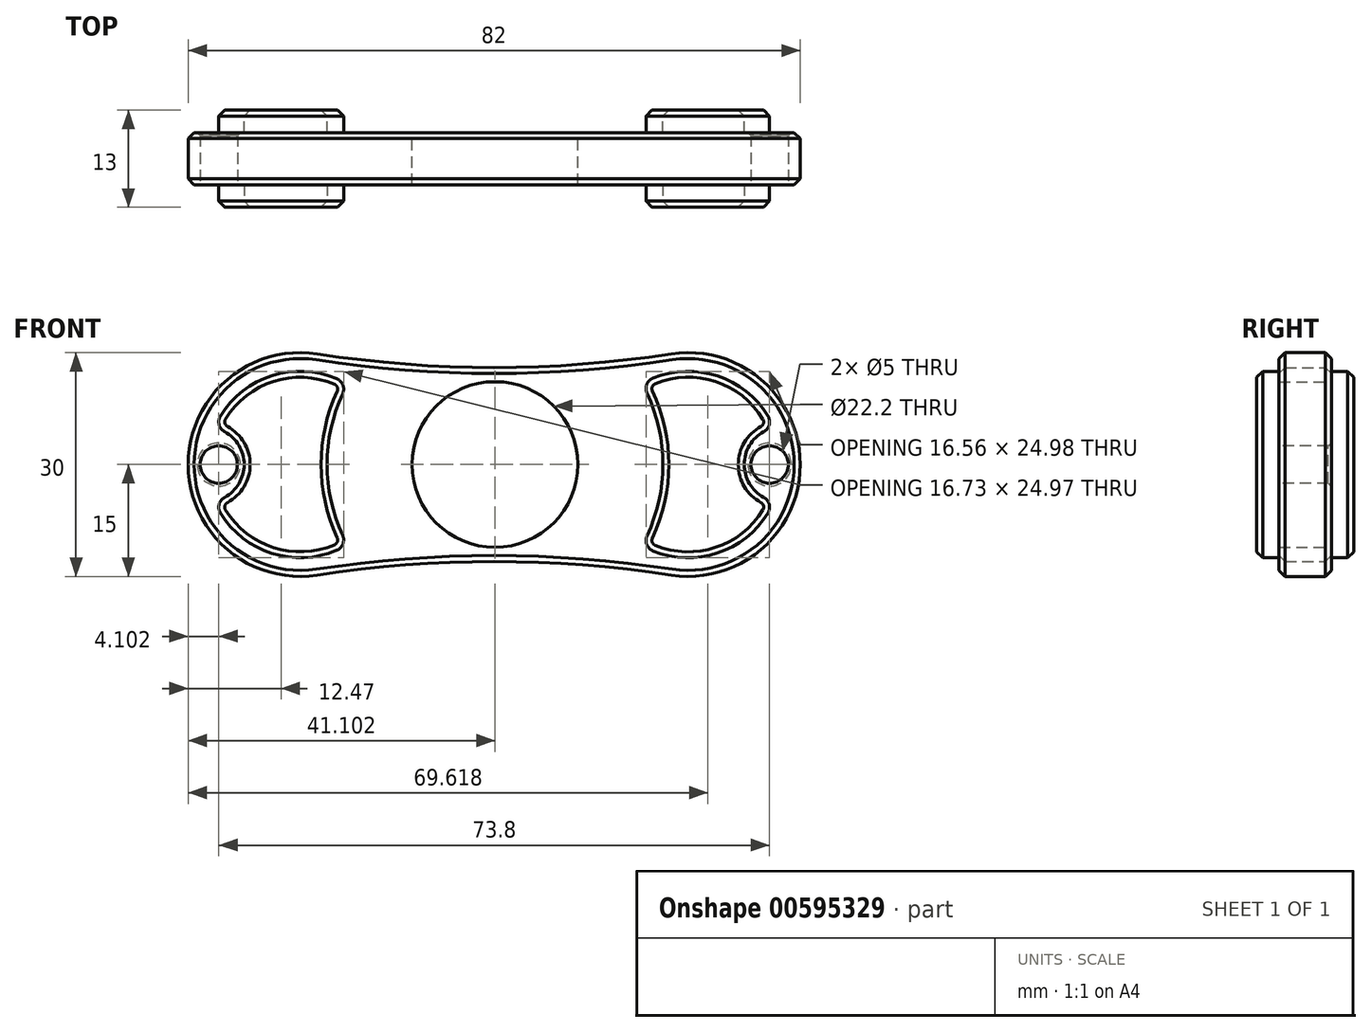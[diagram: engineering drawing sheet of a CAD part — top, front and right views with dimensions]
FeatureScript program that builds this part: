
annotation { "Feature Type Name" : "Feature", "Feature Type Description" : "" }
export const myFeature = defineFeature(function(context is Context, id is Id, definition is map)
    precondition{}
    {
        {
            var Q0;
            Q0=qCreatedBy(makeId("Front.planeOp"),FACE);
            var sketch = newSketch(context, id + "F0", { "sketchPlane" : qUnion([Q0])});
            skCircle(sketch, "E0", {"center": v(-1.84, 0) * mm, "radius": 11.1 * mm});
            skArc(sketch, "E1", {"start": v(-25.64, 14.82) * mm, "mid": v(-42.94, 0) * mm, "end": v(-25.64, -14.82) * mm});
            skArc(sketch, "E2", {"start": v(-25.64, 14.82) * mm, "mid": v(-1.94, 13) * mm, "end": v(21.77, 14.82) * mm});
            skArc(sketch, "E3", {"start": v(21.77, -14.82) * mm, "mid": v(-1.94, -13) * mm, "end": v(-25.64, -14.82) * mm});
            skArc(sketch, "E4.trimOffspring", {"start": v(21.77, -14.82) * mm, "mid": v(39.06, 0) * mm, "end": v(21.77, 14.82) * mm});
            skSolve(sketch);
        }
        {
            var Q0;
            Q0=makeQuery(id+"F0.imprint","IMPRINT",FACE,{"disambiguationData":[TD([[makeQuery(id+"F0.imprint","IMPRINT",EDGE,{"derivedFrom":sQuery(id+"F0.wireOp",EDGE,"E0")}),-1.0]])]});
            extrude(context, id + "F1", {"entities" : qUnion([Q0]), "depth" : 7 * mm, "offsetDistance" : 25 * mm});
        }
        {
            var Q0;
            Q0=makeQuery(id+"F1.opExtrude","CAP_EDGE",EDGE,{"disambiguationData":[OSD([sQuery(id+"F0.wireOp",EDGE,"E1")])],"isStart":false});
            var Q1;
            Q1=makeQuery(id+"F1.opExtrude","CAP_EDGE",EDGE,{"disambiguationData":[OSD([sQuery(id+"F0.wireOp",EDGE,"E3")])],"isStart":false});
            var Q2;
            Q2=makeQuery(id+"F1.opExtrude","CAP_EDGE",EDGE,{"disambiguationData":[OSD([sQuery(id+"F0.wireOp",EDGE,"E3")])],"isStart":true});
            chamfer(context, id + "F2", {"entities" : qUnion([Q0, Q1, Q2]), "width" : .8 * mm, "tangentPropagation" : true});
        }
        {
            var Q0;
            Q0=makeQuery(id+"F1.opExtrude","CAP_FACE",FACE,{"disambiguationData":[OSD([sQuery(id+"F0.wireOp",EDGE,"E0"),sQuery(id+"F0.wireOp",EDGE,"E1"),sQuery(id+"F0.wireOp",EDGE,"E2"),sQuery(id+"F0.wireOp",EDGE,"E3"),sQuery(id+"F0.wireOp",EDGE,"E4.trimOffspring")])],"isStart":false});
            var sketch = newSketch(context, id + "F3", { "sketchPlane" : qUnion([Q0])});
            skCircle(sketch, "E5", {"center": v(-27.94, 0) * mm, "radius": 12.5 * mm});
            skCircle(sketch, "E6", {"center": v(24.06, 0) * mm, "radius": 12.5 * mm});
            skSolve(sketch);
        }
        {
            var Q0;
            Q0=qSketchRegion(id+"F3",true);
            extrude(context, id + "F4", {"entities" : qUnion([Q0]), "operationType" : NewBodyOperationType.ADD, "depth" : 3 * mm, "offsetDistance" : 25 * mm});
        }
        {
            var Q0;
            Q0=makeQuery(id+"F1.opExtrude","CAP_FACE",FACE,{"disambiguationData":[OSD([sQuery(id+"F0.wireOp",EDGE,"E0"),sQuery(id+"F0.wireOp",EDGE,"E1"),sQuery(id+"F0.wireOp",EDGE,"E2"),sQuery(id+"F0.wireOp",EDGE,"E3"),sQuery(id+"F0.wireOp",EDGE,"E4.trimOffspring")])],"isStart":true});
            var sketch = newSketch(context, id + "F5", { "sketchPlane" : qUnion([Q0])});
            skCircle(sketch, "E7", {"center": v(-24.06, 0) * mm, "radius": 12.5 * mm});
            skCircle(sketch, "E8", {"center": v(27.94, 0) * mm, "radius": 12.5 * mm});
            skSolve(sketch);
        }
        {
            var Q0;
            Q0=qSketchRegion(id+"F5",true);
            extrude(context, id + "F6", {"entities" : qUnion([Q0]), "operationType" : NewBodyOperationType.ADD, "depth" : 3 * mm, "offsetDistance" : 25 * mm});
        }
        {
            var Q0;
            Q0=makeQuery(id+"F4.opExtrude","CAP_FACE",FACE,{"disambiguationData":[OSD([sQuery(id+"F3.wireOp",EDGE,"E6")])],"isStart":false});
            var sketch = newSketch(context, id + "F7", { "sketchPlane" : qUnion([Q0])});
            skSolve(sketch);
        }
        {
            var Q0;
            Q0=makeQuery(id+"F4.opExtrude","CAP_FACE",FACE,{"disambiguationData":[OSD([sQuery(id+"F3.wireOp",EDGE,"E5")])],"isStart":false});
            var sketch = newSketch(context, id + "F8", { "sketchPlane" : qUnion([Q0])});
            skCircle(sketch, "E9", {"center": v(-1.84, 0) * mm, "radius": 22.5 * mm});
            skSolve(sketch);
        }
        {
            var Q0;
            Q0=qSketchRegion(id+"F8",true);
            extrude(context, id + "F9", {"entities" : qUnion([Q0]), "operationType" : NewBodyOperationType.REMOVE, "oppositeDirection" : true, "depth" : 3 * mm, "offsetDistance" : 25 * mm});
        }
        {
            var Q0;
            Q0=makeQuery(id+"F6.opExtrude","CAP_FACE",FACE,{"disambiguationData":[OSD([sQuery(id+"F5.wireOp",EDGE,"E7")])],"isStart":false});
            var sketch = newSketch(context, id + "F10", { "sketchPlane" : qUnion([Q0])});
            skCircle(sketch, "E10", {"center": v(1.84, 0) * mm, "radius": 22.5 * mm});
            skSolve(sketch);
        }
        {
            var Q0;
            Q0=qSketchRegion(id+"F10",true);
            extrude(context, id + "F11", {"entities" : qUnion([Q0]), "operationType" : NewBodyOperationType.REMOVE, "oppositeDirection" : true, "depth" : 3 * mm, "offsetDistance" : 25 * mm});
        }
        {
            var Q0;
            Q0=makeQuery(id+"F6.opExtrude","CAP_FACE",FACE,{"disambiguationData":[OSD([sQuery(id+"F5.wireOp",EDGE,"E7")])],"isStart":false});
            var sketch = newSketch(context, id + "F12", { "sketchPlane" : qUnion([Q0])});
            skCircle(sketch, "E11", {"center": v(-36.56, 0) * mm, "radius": 5 * mm});
            skSolve(sketch);
        }
        {
            var Q0;
            Q0=qSketchRegion(id+"F12",true);
            extrude(context, id + "F13", {"entities" : qUnion([Q0]), "operationType" : NewBodyOperationType.REMOVE, "oppositeDirection" : true, "depth" : 3 * mm, "offsetDistance" : 25 * mm});
        }
        {
            var Q0;
            Q0=makeQuery(id+"F6.opExtrude","CAP_FACE",FACE,{"disambiguationData":[OSD([sQuery(id+"F5.wireOp",EDGE,"E8")])],"isStart":false});
            var sketch = newSketch(context, id + "F14", { "sketchPlane" : qUnion([Q0])});
            skCircle(sketch, "E12", {"center": v(40.44, 0) * mm, "radius": 5 * mm});
            skSolve(sketch);
        }
        {
            var Q0;
            Q0=qSketchRegion(id+"F14",true);
            extrude(context, id + "F15", {"entities" : qUnion([Q0]), "operationType" : NewBodyOperationType.REMOVE, "oppositeDirection" : true, "depth" : 3 * mm, "offsetDistance" : 25 * mm});
        }
        {
            var Q0;
            Q0=makeQuery(id+"F4.opExtrude","CAP_FACE",FACE,{"disambiguationData":[OSD([sQuery(id+"F3.wireOp",EDGE,"E5")])],"isStart":false});
            var sketch = newSketch(context, id + "F16", { "sketchPlane" : qUnion([Q0])});
            skCircle(sketch, "E13", {"center": v(-40.44, 0) * mm, "radius": 5 * mm});
            skSolve(sketch);
        }
        {
            var Q0;
            Q0=qSketchRegion(id+"F16",true);
            extrude(context, id + "F17", {"entities" : qUnion([Q0]), "operationType" : NewBodyOperationType.REMOVE, "oppositeDirection" : true, "depth" : 3 * mm, "offsetDistance" : 25 * mm});
        }
        {
            var Q0;
            Q0=makeQuery(id+"F7.imprint","IMPRINT",FACE,{"disambiguationData":[TD([[makeQuery(id+"F7.imprint","IMPRINT",EDGE,{"derivedFrom":makeQuery(id+"F4.opExtrude","CAP_EDGE",EDGE,{"disambiguationData":[OSD([sQuery(id+"F3.wireOp",EDGE,"E6")])],"isStart":false})}),1.0]])]});
            var sketch = newSketch(context, id + "F18", { "sketchPlane" : qUnion([Q0])});
            skCircle(sketch, "E14", {"center": v(36.56, 0) * mm, "radius": 5 * mm});
            skSolve(sketch);
        }
        {
            var Q0;
            Q0=qSketchRegion(id+"F18",true);
            extrude(context, id + "F19", {"entities" : qUnion([Q0]), "operationType" : NewBodyOperationType.REMOVE, "oppositeDirection" : true, "depth" : 3 * mm, "offsetDistance" : 25 * mm});
        }
        {
            var Q0;
            Q0=makeQuery(id+"F17.boolean.opBoolean","INTERSECT",EDGE,{"disambiguationData":[OD(0.0)],"derivedFrom":[makeQuery(id+"F4.opExtrude","SWEPT_FACE",FACE,{"disambiguationData":[OSD([sQuery(id+"F3.wireOp",EDGE,"E5")])]}),makeQuery(id+"F17.opExtrude","SWEPT_FACE",FACE,{"disambiguationData":[OSD([sQuery(id+"F16.wireOp",EDGE,"E13")])]})]});
            var Q1;
            Q1=makeQuery(id+"F17.boolean.opBoolean","INTERSECT",EDGE,{"disambiguationData":[OD(1.0)],"derivedFrom":[makeQuery(id+"F4.opExtrude","SWEPT_FACE",FACE,{"disambiguationData":[OSD([sQuery(id+"F3.wireOp",EDGE,"E5")])]}),makeQuery(id+"F17.opExtrude","SWEPT_FACE",FACE,{"disambiguationData":[OSD([sQuery(id+"F16.wireOp",EDGE,"E13")])]})]});
            var Q2;
            Q2=makeQuery(id+"F9.boolean.opBoolean","INTERSECT",EDGE,{"disambiguationData":[OD(1.0)],"derivedFrom":[makeQuery(id+"F4.opExtrude","SWEPT_FACE",FACE,{"disambiguationData":[OSD([sQuery(id+"F3.wireOp",EDGE,"E5")])]}),makeQuery(id+"F9.opExtrude","SWEPT_FACE",FACE,{"disambiguationData":[OSD([sQuery(id+"F8.wireOp",EDGE,"E9")])]})]});
            var Q3;
            Q3=makeQuery(id+"F9.boolean.opBoolean","INTERSECT",EDGE,{"disambiguationData":[OD(0.0)],"derivedFrom":[makeQuery(id+"F4.opExtrude","SWEPT_FACE",FACE,{"disambiguationData":[OSD([sQuery(id+"F3.wireOp",EDGE,"E5")])]}),makeQuery(id+"F9.opExtrude","SWEPT_FACE",FACE,{"disambiguationData":[OSD([sQuery(id+"F8.wireOp",EDGE,"E9")])]})]});
            var Q4;
            Q4=makeQuery(id+"F9.boolean.opBoolean","INTERSECT",EDGE,{"disambiguationData":[OD(1.0)],"derivedFrom":[makeQuery(id+"F4.opExtrude","SWEPT_FACE",FACE,{"disambiguationData":[OSD([sQuery(id+"F3.wireOp",EDGE,"E6")])]}),makeQuery(id+"F9.opExtrude","SWEPT_FACE",FACE,{"disambiguationData":[OSD([sQuery(id+"F8.wireOp",EDGE,"E9")])]})]});
            var Q5;
            Q5=makeQuery(id+"F9.boolean.opBoolean","INTERSECT",EDGE,{"disambiguationData":[OD(0.0)],"derivedFrom":[makeQuery(id+"F4.opExtrude","SWEPT_FACE",FACE,{"disambiguationData":[OSD([sQuery(id+"F3.wireOp",EDGE,"E6")])]}),makeQuery(id+"F9.opExtrude","SWEPT_FACE",FACE,{"disambiguationData":[OSD([sQuery(id+"F8.wireOp",EDGE,"E9")])]})]});
            var Q6;
            Q6=makeQuery(id+"F19.boolean.opBoolean","INTERSECT",EDGE,{"disambiguationData":[OD(1.0)],"derivedFrom":[makeQuery(id+"F4.opExtrude","SWEPT_FACE",FACE,{"disambiguationData":[OSD([sQuery(id+"F3.wireOp",EDGE,"E6")])]}),makeQuery(id+"F19.opExtrude","SWEPT_FACE",FACE,{"disambiguationData":[OSD([sQuery(id+"F18.wireOp",EDGE,"E14")])]})]});
            var Q7;
            Q7=makeQuery(id+"F19.boolean.opBoolean","INTERSECT",EDGE,{"disambiguationData":[OD(0.0)],"derivedFrom":[makeQuery(id+"F4.opExtrude","SWEPT_FACE",FACE,{"disambiguationData":[OSD([sQuery(id+"F3.wireOp",EDGE,"E6")])]}),makeQuery(id+"F19.opExtrude","SWEPT_FACE",FACE,{"disambiguationData":[OSD([sQuery(id+"F18.wireOp",EDGE,"E14")])]})]});
            var Q8;
            Q8=makeQuery(id+"F11.boolean.opBoolean","INTERSECT",EDGE,{"disambiguationData":[OD(0.0)],"derivedFrom":[makeQuery(id+"F6.opExtrude","SWEPT_FACE",FACE,{"disambiguationData":[OSD([sQuery(id+"F5.wireOp",EDGE,"E8")])]}),makeQuery(id+"F11.opExtrude","SWEPT_FACE",FACE,{"disambiguationData":[OSD([sQuery(id+"F10.wireOp",EDGE,"E10")])]})]});
            var Q9;
            Q9=makeQuery(id+"F11.boolean.opBoolean","INTERSECT",EDGE,{"disambiguationData":[OD(1.0)],"derivedFrom":[makeQuery(id+"F6.opExtrude","SWEPT_FACE",FACE,{"disambiguationData":[OSD([sQuery(id+"F5.wireOp",EDGE,"E8")])]}),makeQuery(id+"F11.opExtrude","SWEPT_FACE",FACE,{"disambiguationData":[OSD([sQuery(id+"F10.wireOp",EDGE,"E10")])]})]});
            var Q10;
            Q10=makeQuery(id+"F15.boolean.opBoolean","INTERSECT",EDGE,{"disambiguationData":[OD(0.0)],"derivedFrom":[makeQuery(id+"F6.opExtrude","SWEPT_FACE",FACE,{"disambiguationData":[OSD([sQuery(id+"F5.wireOp",EDGE,"E8")])]}),makeQuery(id+"F15.opExtrude","SWEPT_FACE",FACE,{"disambiguationData":[OSD([sQuery(id+"F14.wireOp",EDGE,"E12")])]})]});
            var Q11;
            Q11=makeQuery(id+"F15.boolean.opBoolean","INTERSECT",EDGE,{"disambiguationData":[OD(1.0)],"derivedFrom":[makeQuery(id+"F6.opExtrude","SWEPT_FACE",FACE,{"disambiguationData":[OSD([sQuery(id+"F5.wireOp",EDGE,"E8")])]}),makeQuery(id+"F15.opExtrude","SWEPT_FACE",FACE,{"disambiguationData":[OSD([sQuery(id+"F14.wireOp",EDGE,"E12")])]})]});
            var Q12;
            Q12=makeQuery(id+"F11.boolean.opBoolean","INTERSECT",EDGE,{"disambiguationData":[OD(0.0)],"derivedFrom":[makeQuery(id+"F6.opExtrude","SWEPT_FACE",FACE,{"disambiguationData":[OSD([sQuery(id+"F5.wireOp",EDGE,"E7")])]}),makeQuery(id+"F11.opExtrude","SWEPT_FACE",FACE,{"disambiguationData":[OSD([sQuery(id+"F10.wireOp",EDGE,"E10")])]})]});
            var Q13;
            Q13=makeQuery(id+"F11.boolean.opBoolean","INTERSECT",EDGE,{"disambiguationData":[OD(1.0)],"derivedFrom":[makeQuery(id+"F6.opExtrude","SWEPT_FACE",FACE,{"disambiguationData":[OSD([sQuery(id+"F5.wireOp",EDGE,"E7")])]}),makeQuery(id+"F11.opExtrude","SWEPT_FACE",FACE,{"disambiguationData":[OSD([sQuery(id+"F10.wireOp",EDGE,"E10")])]})]});
            var Q14;
            Q14=makeQuery(id+"F13.boolean.opBoolean","INTERSECT",EDGE,{"disambiguationData":[OD(0.0)],"derivedFrom":[makeQuery(id+"F6.opExtrude","SWEPT_FACE",FACE,{"disambiguationData":[OSD([sQuery(id+"F5.wireOp",EDGE,"E7")])]}),makeQuery(id+"F13.opExtrude","SWEPT_FACE",FACE,{"disambiguationData":[OSD([sQuery(id+"F12.wireOp",EDGE,"E11")])]})]});
            var Q15;
            Q15=makeQuery(id+"F13.boolean.opBoolean","INTERSECT",EDGE,{"disambiguationData":[OD(1.0)],"derivedFrom":[makeQuery(id+"F6.opExtrude","SWEPT_FACE",FACE,{"disambiguationData":[OSD([sQuery(id+"F5.wireOp",EDGE,"E7")])]}),makeQuery(id+"F13.opExtrude","SWEPT_FACE",FACE,{"disambiguationData":[OSD([sQuery(id+"F12.wireOp",EDGE,"E11")])]})]});
            fillet(context, id + "F20", {"entities" : qUnion([Q0, Q1, Q2, Q3, Q4, Q5, Q6, Q7, Q8, Q9, Q10, Q11, Q12, Q13, Q14, Q15]), "radius" : 1.5 * mm, "tangentPropagation" : true, "allowEdgeOverflow" : false});
        }
        {
            var Q0;
            Q0=makeQuery(id+"F19.boolean.opBoolean","MERGE",FACE,{"derivedFrom":[makeQuery(id+"F17.boolean.opBoolean","MERGE",FACE,{"derivedFrom":[makeQuery(id+"F9.boolean.opBoolean","MERGE",FACE,{"derivedFrom":[makeQuery(id+"F1.opExtrude","CAP_FACE",FACE,{"disambiguationData":[OSD([sQuery(id+"F0.wireOp",EDGE,"E0"),sQuery(id+"F0.wireOp",EDGE,"E1"),sQuery(id+"F0.wireOp",EDGE,"E2"),sQuery(id+"F0.wireOp",EDGE,"E3"),sQuery(id+"F0.wireOp",EDGE,"E4.trimOffspring")])],"isStart":false}),makeQuery(id+"F9.opExtrude","CAP_FACE",FACE,{"disambiguationData":[OSD([sQuery(id+"F8.wireOp",EDGE,"E9")])],"isStart":false})]}),makeQuery(id+"F17.opExtrude","CAP_FACE",FACE,{"disambiguationData":[OSD([sQuery(id+"F16.wireOp",EDGE,"E13")])],"isStart":false})]}),makeQuery(id+"F19.opExtrude","CAP_FACE",FACE,{"disambiguationData":[OSD([sQuery(id+"F18.wireOp",EDGE,"E14")])],"isStart":false})]});
            var sketch = newSketch(context, id + "F21", { "sketchPlane" : qUnion([Q0])});
            skCircle(sketch, "E15", {"center": v(-38.84, 0) * mm, "radius": 2.5 * mm});
            skSolve(sketch);
        }
        {
            var Q0;
            Q0=qSketchRegion(id+"F21",true);
            extrude(context, id + "F22", {"entities" : qUnion([Q0]), "operationType" : NewBodyOperationType.REMOVE, "oppositeDirection" : true, "depth" : 25 * mm, "offsetDistance" : 25 * mm});
        }
        {
            var Q0;
            Q0=makeQuery(id+"F19.boolean.opBoolean","MERGE",FACE,{"derivedFrom":[makeQuery(id+"F17.boolean.opBoolean","MERGE",FACE,{"derivedFrom":[makeQuery(id+"F9.boolean.opBoolean","MERGE",FACE,{"derivedFrom":[makeQuery(id+"F1.opExtrude","CAP_FACE",FACE,{"disambiguationData":[OSD([sQuery(id+"F0.wireOp",EDGE,"E0"),sQuery(id+"F0.wireOp",EDGE,"E1"),sQuery(id+"F0.wireOp",EDGE,"E2"),sQuery(id+"F0.wireOp",EDGE,"E3"),sQuery(id+"F0.wireOp",EDGE,"E4.trimOffspring")])],"isStart":false}),makeQuery(id+"F9.opExtrude","CAP_FACE",FACE,{"disambiguationData":[OSD([sQuery(id+"F8.wireOp",EDGE,"E9")])],"isStart":false})]}),makeQuery(id+"F17.opExtrude","CAP_FACE",FACE,{"disambiguationData":[OSD([sQuery(id+"F16.wireOp",EDGE,"E13")])],"isStart":false})]}),makeQuery(id+"F19.opExtrude","CAP_FACE",FACE,{"disambiguationData":[OSD([sQuery(id+"F18.wireOp",EDGE,"E14")])],"isStart":false})]});
            var sketch = newSketch(context, id + "F23", { "sketchPlane" : qUnion([Q0])});
            skCircle(sketch, "E16", {"center": v(34.96, 0) * mm, "radius": 2.5 * mm});
            skSolve(sketch);
        }
        {
            var Q0;
            Q0=qSketchRegion(id+"F23",true);
            extrude(context, id + "F24", {"entities" : qUnion([Q0]), "operationType" : NewBodyOperationType.REMOVE, "oppositeDirection" : true, "depth" : 25 * mm, "offsetDistance" : 25 * mm});
        }
        {
            var Q0;
            Q0=makeQuery(id+"F22.boolean.opBoolean","COPY",EDGE,{"derivedFrom":makeQuery(id+"F22.opExtrude","CAP_EDGE",EDGE,{"disambiguationData":[OSD([sQuery(id+"F21.wireOp",EDGE,"E15")])],"isStart":true})});
            var Q1;
            Q1=makeQuery(id+"F24.boolean.opBoolean","COPY",EDGE,{"derivedFrom":makeQuery(id+"F24.opExtrude","CAP_EDGE",EDGE,{"disambiguationData":[OSD([sQuery(id+"F23.wireOp",EDGE,"E16")])],"isStart":true})});
            var Q2;
            Q2=makeQuery(id+"F24.boolean.opBoolean","INTERSECT",EDGE,{"derivedFrom":[makeQuery(id+"F15.boolean.opBoolean","MERGE",FACE,{"derivedFrom":[makeQuery(id+"F13.boolean.opBoolean","MERGE",FACE,{"derivedFrom":[makeQuery(id+"F11.boolean.opBoolean","MERGE",FACE,{"derivedFrom":[makeQuery(id+"F1.opExtrude","CAP_FACE",FACE,{"disambiguationData":[OSD([sQuery(id+"F0.wireOp",EDGE,"E0"),sQuery(id+"F0.wireOp",EDGE,"E1"),sQuery(id+"F0.wireOp",EDGE,"E2"),sQuery(id+"F0.wireOp",EDGE,"E3"),sQuery(id+"F0.wireOp",EDGE,"E4.trimOffspring")])],"isStart":true}),makeQuery(id+"F11.opExtrude","CAP_FACE",FACE,{"disambiguationData":[OSD([sQuery(id+"F10.wireOp",EDGE,"E10")])],"isStart":false})]}),makeQuery(id+"F13.opExtrude","CAP_FACE",FACE,{"disambiguationData":[OSD([sQuery(id+"F12.wireOp",EDGE,"E11")])],"isStart":false})]}),makeQuery(id+"F15.opExtrude","CAP_FACE",FACE,{"disambiguationData":[OSD([sQuery(id+"F14.wireOp",EDGE,"E12")])],"isStart":false})]}),makeQuery(id+"F24.opExtrude","SWEPT_FACE",FACE,{"disambiguationData":[OSD([sQuery(id+"F23.wireOp",EDGE,"E16")])]})]});
            var Q3;
            Q3=makeQuery(id+"F22.boolean.opBoolean","INTERSECT",EDGE,{"derivedFrom":[makeQuery(id+"F15.boolean.opBoolean","MERGE",FACE,{"derivedFrom":[makeQuery(id+"F13.boolean.opBoolean","MERGE",FACE,{"derivedFrom":[makeQuery(id+"F11.boolean.opBoolean","MERGE",FACE,{"derivedFrom":[makeQuery(id+"F1.opExtrude","CAP_FACE",FACE,{"disambiguationData":[OSD([sQuery(id+"F0.wireOp",EDGE,"E0"),sQuery(id+"F0.wireOp",EDGE,"E1"),sQuery(id+"F0.wireOp",EDGE,"E2"),sQuery(id+"F0.wireOp",EDGE,"E3"),sQuery(id+"F0.wireOp",EDGE,"E4.trimOffspring")])],"isStart":true}),makeQuery(id+"F11.opExtrude","CAP_FACE",FACE,{"disambiguationData":[OSD([sQuery(id+"F10.wireOp",EDGE,"E10")])],"isStart":false})]}),makeQuery(id+"F13.opExtrude","CAP_FACE",FACE,{"disambiguationData":[OSD([sQuery(id+"F12.wireOp",EDGE,"E11")])],"isStart":false})]}),makeQuery(id+"F15.opExtrude","CAP_FACE",FACE,{"disambiguationData":[OSD([sQuery(id+"F14.wireOp",EDGE,"E12")])],"isStart":false})]}),makeQuery(id+"F22.opExtrude","SWEPT_FACE",FACE,{"disambiguationData":[OSD([sQuery(id+"F21.wireOp",EDGE,"E15")])]})]});
            chamfer(context, id + "F25", {"entities" : qUnion([Q0, Q1, Q2, Q3]), "width" : 0.4 * mm, "tangentPropagation" : true});
        }
        {
            var Q0;
            Q0=makeQuery(id+"F4.opExtrude","CAP_FACE",FACE,{"disambiguationData":[OSD([sQuery(id+"F3.wireOp",EDGE,"E6")])],"isStart":false});
            var Q1;
            Q1=makeQuery(id+"F4.opExtrude","CAP_FACE",FACE,{"disambiguationData":[OSD([sQuery(id+"F3.wireOp",EDGE,"E5")])],"isStart":false});
            var Q2;
            Q2=makeQuery(id+"F6.opExtrude","CAP_FACE",FACE,{"disambiguationData":[OSD([sQuery(id+"F5.wireOp",EDGE,"E8")])],"isStart":false});
            var Q3;
            Q3=makeQuery(id+"F6.opExtrude","CAP_FACE",FACE,{"disambiguationData":[OSD([sQuery(id+"F5.wireOp",EDGE,"E7")])],"isStart":false});
            chamfer(context, id + "F26", {"entities" : qUnion([Q0, Q1, Q2, Q3]), "width" : .8 * mm, "tangentPropagation" : true});
        }
    });
